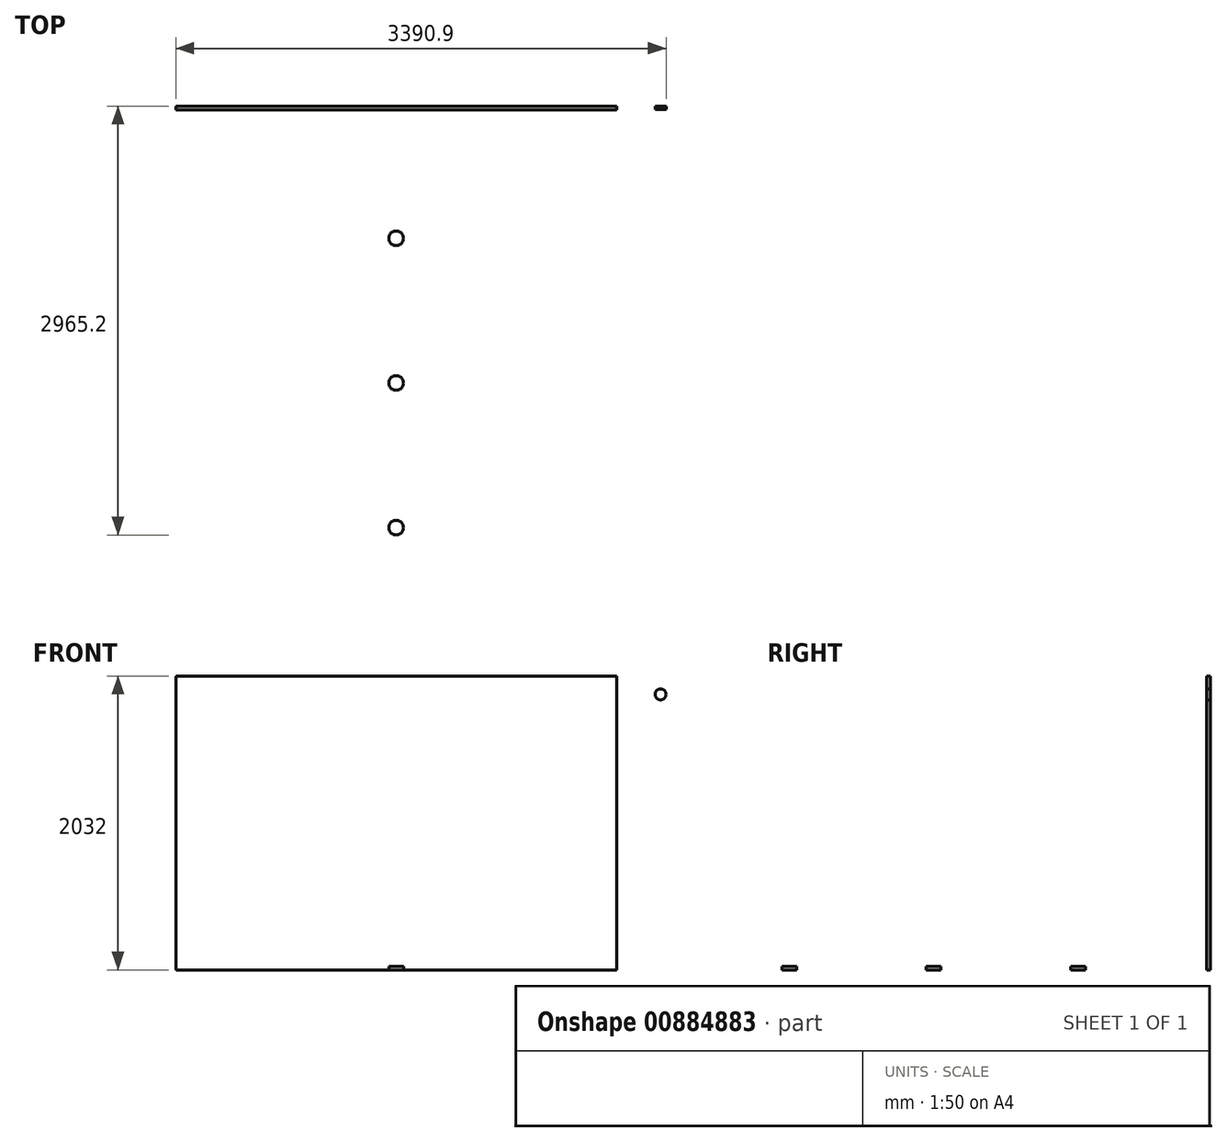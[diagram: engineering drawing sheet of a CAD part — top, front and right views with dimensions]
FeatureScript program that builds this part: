
annotation { "Feature Type Name" : "Feature", "Feature Type Description" : "" }
export const myFeature = defineFeature(function(context is Context, id is Id, definition is map)
    precondition{}
    {
        {
            var Q0;
            Q0=qCreatedBy(makeId("Front.planeOp"),FACE);
            var sketch = newSketch(context, id + "F0", { "sketchPlane" : qUnion([Q0])});
            skLineSegment(sketch, "E0.bottom", {"start": v(-1524, 0) * mm, "end": v(1524, 0) * mm});
            skLineSegment(sketch, "E0.top", {"start": v(-1524, 2032) * mm, "end": v(1524, 2032) * mm});
            skLineSegment(sketch, "E0.left", {"start": v(-1524, 0) * mm, "end": v(-1524, 2032) * mm});
            skLineSegment(sketch, "E0.right", {"start": v(1524, 0) * mm, "end": v(1524, 2032) * mm});
            skPoint(sketch, "E0.middle", {"position": v(0, 1016) * mm});
            skSolve(sketch);
        }
        {
            var Q0;
            Q0=makeQuery(id+"F0.imprint","IMPRINT",FACE,{"disambiguationData":[TD([[makeQuery(id+"F0.imprint","IMPRINT",EDGE,{"derivedFrom":sQuery(id+"F0.wireOp",EDGE,"E0.bottom")}),1.0]])]});
            extrude(context, id + "F1", {"entities" : qUnion([Q0]), "depth" : 25.4 * mm, "offsetDistance" : 25 * mm});
        }
        {
            var Q0;
            Q0=qCreatedBy(makeId("Front.planeOp"),FACE);
            var sketch = newSketch(context, id + "F2", { "sketchPlane" : qUnion([Q0])});
            skCircle(sketch, "E1", {"center": v(1828.8, 1905) * mm, "radius": 38.1 * mm});
            skSolve(sketch);
        }
        {
            var Q0;
            Q0=makeQuery(id+"F2.imprint","IMPRINT",FACE,{"disambiguationData":[TD([[makeQuery(id+"F2.imprint","IMPRINT",EDGE,{"derivedFrom":sQuery(id+"F2.wireOp",EDGE,"E1")}),1.0]])]});
            extrude(context, id + "F3", {"entities" : qUnion([Q0]), "depth" : 25 * mm, "offsetDistance" : 25 * mm});
        }
        {
            var Q0;
            Q0=qCreatedBy(makeId("Top.planeOp"),FACE);
            var sketch = newSketch(context, id + "F4", { "sketchPlane" : qUnion([Q0])});
            skCircle(sketch, "E2", {"center": v(0, -914.4) * mm, "radius": 50.8 * mm});
            skCircle(sketch, "E3", {"center": v(0, -1914.4) * mm, "radius": 50.8 * mm});
            skCircle(sketch, "E4", {"center": v(0, -2914.4) * mm, "radius": 50.8 * mm});
            skSolve(sketch);
        }
        {
            var Q0;
            Q0=makeQuery(id+"F4.imprint","IMPRINT",FACE,{"disambiguationData":[TD([[makeQuery(id+"F4.imprint","IMPRINT",EDGE,{"derivedFrom":sQuery(id+"F4.wireOp",EDGE,"E4")}),1.0]])]});
            var Q1;
            Q1=makeQuery(id+"F4.imprint","IMPRINT",FACE,{"disambiguationData":[TD([[makeQuery(id+"F4.imprint","IMPRINT",EDGE,{"derivedFrom":sQuery(id+"F4.wireOp",EDGE,"E3")}),1.0]])]});
            var Q2;
            Q2=makeQuery(id+"F4.imprint","IMPRINT",FACE,{"disambiguationData":[TD([[makeQuery(id+"F4.imprint","IMPRINT",EDGE,{"derivedFrom":sQuery(id+"F4.wireOp",EDGE,"E2")}),1.0]])]});
            extrude(context, id + "F5", {"entities" : qUnion([Q0, Q1, Q2]), "depth" : 25 * mm, "offsetDistance" : 25 * mm});
        }
    });
